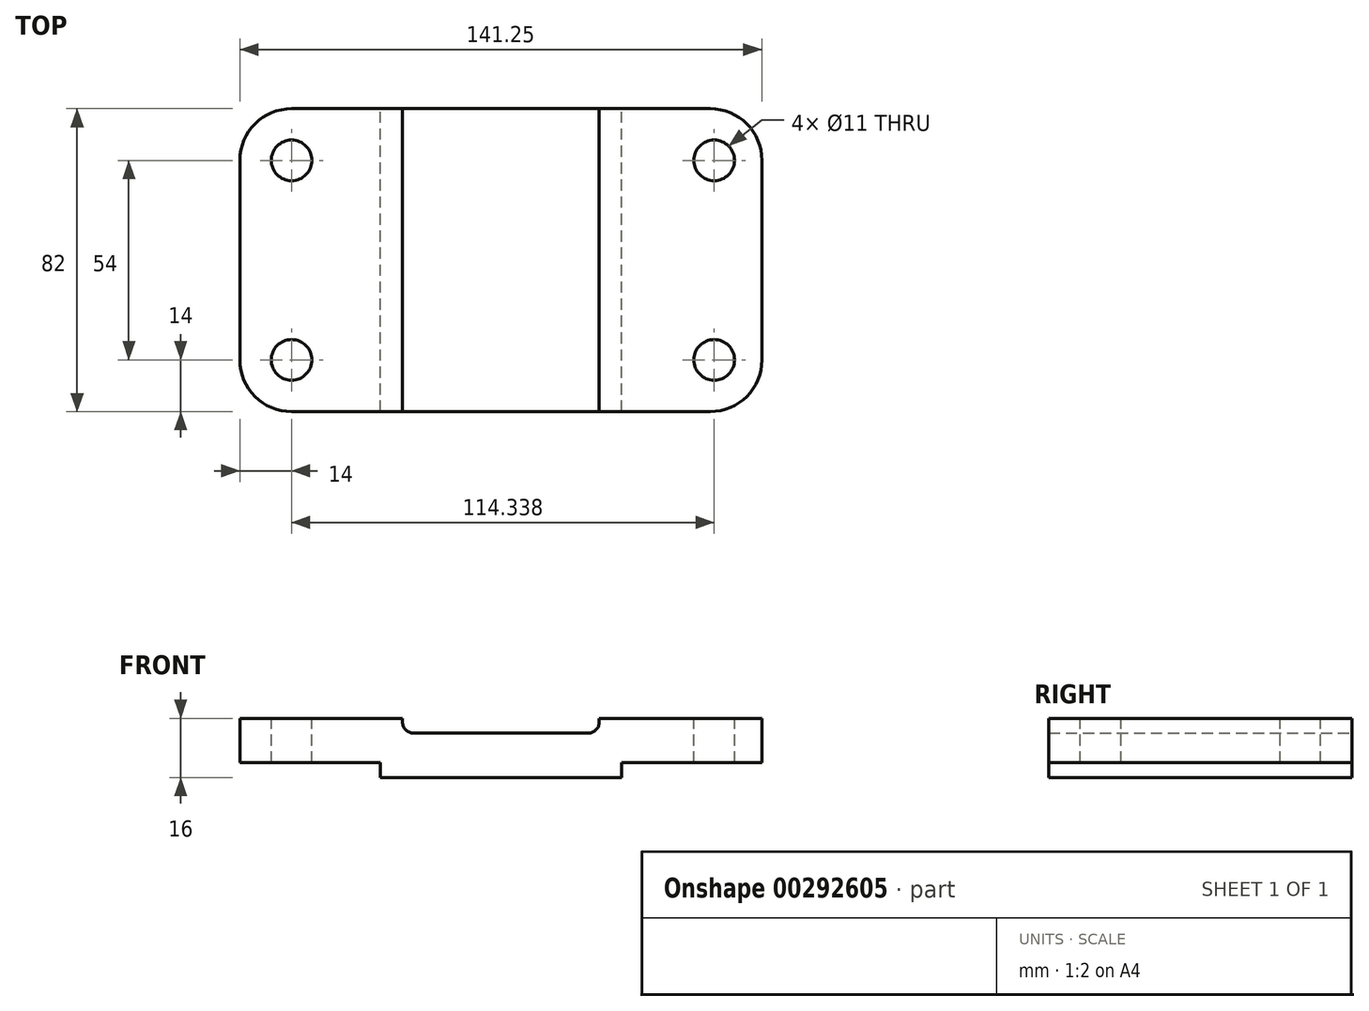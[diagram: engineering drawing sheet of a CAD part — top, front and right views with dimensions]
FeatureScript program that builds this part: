
annotation { "Feature Type Name" : "Feature", "Feature Type Description" : "" }
export const myFeature = defineFeature(function(context is Context, id is Id, definition is map)
    precondition{}
    {
        {
            var Q0;
            Q0=qCreatedBy(makeId("Front.planeOp"),FACE);
            var sketch = newSketch(context, id + "F0", { "sketchPlane" : qUnion([Q0])});
            skLineSegment(sketch, "E0", {"start": v(0, 0) * mm, "end": v(0, 12) * mm});
            skLineSegment(sketch, "E1", {"start": v(0, 12) * mm, "end": v(44, 12) * mm});
            skLineSegment(sketch, "E2", {"start": v(44, 12) * mm, "end": v(44, 8) * mm});
            skLineSegment(sketch, "E3", {"start": v(44, 8) * mm, "end": v(97.25, 8) * mm});
            skLineSegment(sketch, "E4", {"start": v(97.25, 8) * mm, "end": v(97.25, 12) * mm});
            skLineSegment(sketch, "E5", {"start": v(97.25, 12) * mm, "end": v(141.25, 12) * mm});
            skLineSegment(sketch, "E6", {"start": v(141.25, 12) * mm, "end": v(141.25, 0) * mm});
            skLineSegment(sketch, "E7", {"start": v(141.25, 0) * mm, "end": v(103.25, 0) * mm});
            skLineSegment(sketch, "E8", {"start": v(103.25, 0) * mm, "end": v(103.25, -4) * mm});
            skLineSegment(sketch, "E9", {"start": v(103.25, -4) * mm, "end": v(38, -4) * mm});
            skLineSegment(sketch, "E10", {"start": v(38, -4) * mm, "end": v(38, 0) * mm});
            skLineSegment(sketch, "E11", {"start": v(38, 0) * mm, "end": v(0, 0) * mm});
            skSolve(sketch);
        }
        {
            var Q0;
            Q0=makeQuery(id+"F0.imprint","IMPRINT",FACE,{"disambiguationData":[TD([[makeQuery(id+"F0.imprint","IMPRINT",EDGE,{"derivedFrom":sQuery(id+"F0.wireOp",EDGE,"E0")}),-1.0]])]});
            extrude(context, id + "F1", {"entities" : qUnion([Q0]), "depth" : 82 * mm});
        }
        {
            var Q0;
            Q0=makeQuery(id+"F1.opExtrude","CAP_EDGE",EDGE,{"disambiguationData":[OSD([sQuery(id+"F0.wireOp",EDGE,"E6")])],"isStart":false});
            var Q1;
            Q1=makeQuery(id+"F1.opExtrude","CAP_EDGE",EDGE,{"disambiguationData":[OSD([sQuery(id+"F0.wireOp",EDGE,"E6")])],"isStart":true});
            var Q2;
            Q2=makeQuery(id+"F1.opExtrude","CAP_EDGE",EDGE,{"disambiguationData":[OSD([sQuery(id+"F0.wireOp",EDGE,"E0")])],"isStart":false});
            var Q3;
            Q3=makeQuery(id+"F1.opExtrude","CAP_EDGE",EDGE,{"disambiguationData":[OSD([sQuery(id+"F0.wireOp",EDGE,"E0")])],"isStart":true});
            fillet(context, id + "F2", {"entities" : qUnion([Q0, Q1, Q2, Q3]), "radius" : 14 * mm, "tangentPropagation" : true, "allowEdgeOverflow" : false});
        }
        {
            var Q0;
            Q0=makeQuery(id+"F1.opExtrude","SWEPT_FACE",FACE,{"disambiguationData":[OSD([sQuery(id+"F0.wireOp",EDGE,"E5")])]});
            var sketch = newSketch(context, id + "F3", { "sketchPlane" : qUnion([Q0])});
            skLineSegment(sketch, "E12", {"start": v(141.25, -14) * mm, "end": v(0, -14) * mm, "construction": true});
            skLineSegment(sketch, "E13", {"start": v(0, -68) * mm, "end": v(141.25, -68) * mm, "construction": true});
            skLineSegment(sketch, "E14", {"start": v(14, -82) * mm, "end": v(14, 0) * mm, "construction": true});
            skLineSegment(sketch, "E15", {"start": v(71.17, -90.52) * mm, "end": v(71.17, 9) * mm, "construction": true});
            skLineSegment(sketch, "E16.MirrorCS", {"start": v(128.34, -82) * mm, "end": v(128.34, 0) * mm, "construction": true});
            skCircle(sketch, "E17", {"center": v(128.34, -68) * mm, "radius": 5.5 * mm});
            skCircle(sketch, "E18", {"center": v(14, -68) * mm, "radius": 5.5 * mm});
            skCircle(sketch, "E19", {"center": v(14, -14) * mm, "radius": 5.5 * mm});
            skCircle(sketch, "E20", {"center": v(128.34, -14) * mm, "radius": 5.5 * mm});
            skSolve(sketch);
        }
        {
            var Q0;
            Q0=makeQuery(id+"F3.imprint","IMPRINT",FACE,{"disambiguationData":[TD([[makeQuery(id+"F3.imprint","IMPRINT",EDGE,{"derivedFrom":sQuery(id+"F3.wireOp",EDGE,"E17")}),1.0]])]});
            var Q1;
            Q1=makeQuery(id+"F3.imprint","IMPRINT",FACE,{"disambiguationData":[TD([[makeQuery(id+"F3.imprint","IMPRINT",EDGE,{"derivedFrom":sQuery(id+"F3.wireOp",EDGE,"E20")}),1.0]])]});
            var Q2;
            Q2=makeQuery(id+"F3.imprint","IMPRINT",FACE,{"disambiguationData":[TD([[makeQuery(id+"F3.imprint","IMPRINT",EDGE,{"derivedFrom":sQuery(id+"F3.wireOp",EDGE,"E18")}),1.0]])]});
            var Q3;
            Q3=makeQuery(id+"F3.imprint","IMPRINT",FACE,{"disambiguationData":[TD([[makeQuery(id+"F3.imprint","IMPRINT",EDGE,{"derivedFrom":sQuery(id+"F3.wireOp",EDGE,"E19")}),1.0]])]});
            extrude(context, id + "F4", {"entities" : qUnion([Q0, Q1, Q2, Q3]), "operationType" : NewBodyOperationType.REMOVE, "endBound" : BoundingType.THROUGH_ALL, "oppositeDirection" : true, "depth" : 25 * mm});
        }
        {
            var Q0;
            Q0=makeQuery(id+"F1.opExtrude","SWEPT_EDGE",EDGE,{"disambiguationData":[OSD([sQuery(id+"F0.wireOp",EDGE,"E2"),sQuery(id+"F0.wireOp",EDGE,"E3")])]});
            var Q1;
            Q1=makeQuery(id+"F1.opExtrude","SWEPT_EDGE",EDGE,{"disambiguationData":[OSD([sQuery(id+"F0.wireOp",EDGE,"E3"),sQuery(id+"F0.wireOp",EDGE,"E4")])]});
            fillet(context, id + "F5", {"entities" : qUnion([Q0, Q1]), "radius" : 3 * mm, "tangentPropagation" : true, "allowEdgeOverflow" : false});
        }
    });
